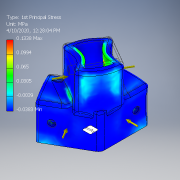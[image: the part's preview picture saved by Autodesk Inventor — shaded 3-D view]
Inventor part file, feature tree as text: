
AUTODESK INVENTOR PART (.ipt)
format: ipt  version: 2019.4 (Build 234330000, 330)  size: 473,600 bytes
history: native  units: mm
features: fillet x12, extrude x8, sketch x8
ambient origin geometry x8: Origin, YZ Plane, XZ Plane, XY Plane, X Axis, Y Axis, Z Axis, Center Point
bodies: Solid1 (feature_tree)
feature tree (28):
  extrude  "Extrusion1"  Depth=40.0mm
  extrude  "Extrusion9"  TaperAngle=60.0deg  [1 undecoded]
  extrude  "Extrusion10"  Depth=30.0mm TaperAngle=0.0deg
  extrude  "Extrusion11"  Depth=21.0mm
  extrude  "Extrusion12"  Depth=21.0mm TaperAngle=0.0deg
  extrude  "Extrusion13"  Depth=21.0mm
  extrude  "Extrusion14"  Depth=21.0mm TaperAngle=0.0deg
  extrude  "Extrusion15"  Depth=5.0mm
  fillet  "Fillet6"  Radius=30.0mm
  fillet  "Fillet7"  Radius=21.0mm
  fillet  "Fillet8"  Radius=21.0mm
  fillet  "Fillet9"  Radius=25.0mm
  fillet  "Fillet10"  Radius=10.0mm
  fillet  "Fillet11"  Radius=5.5mm
  fillet  "Fillet12"  Radius=30.0mm
  fillet  "Fillet13"  Radius=10.0mm
  fillet  "Fillet14"  Radius=5.5mm
  fillet  "Fillet15"  Radius=30.0mm
  fillet  "Fillet16"  Radius=10.0mm
  fillet  "Fillet17"  Radius=5.5mm
  sketch  "Sketch1"  dims[d1=30.0mm d2=40.0mm]
  sketch  "Sketch9"  dims[d3=30.0mm d4=60.0deg]
  sketch  "Sketch10"  dims[d5=40.0mm d6=30.0mm d7=0.0mm]
  sketch  "Sketch11"  dims[d41=15.0mm d42=21.0mm]
  sketch  "Sketch12"  dims[d43=21.0mm d44=25.0mm d45=0.0mm]
  sketch  "Sketch13"  dims[d46=15.0mm d47=21.0mm]
  sketch  "Sketch14"  dims[d48=21.0mm d49=25.0mm d50=0.0mm]
  sketch  "Sketch15"  dims[d51=30.0mm d52=30.0mm d53=30.0mm d54=0.0mm d55=21.0mm d56=21.0mm d57=25.0mm d58=0.0mm d59=10.0mm d60=5.5mm d61=30.0mm d62=0.0mm d63=10.0mm d64=5.5mm d65=30.0mm d66=0.0mm d67=10.0mm d68=5.5mm d69=30.0mm d70=0.0mm d71=5.0mm d72=5.0mm d73=5.0mm d74=5.0mm d75=2.0mm d76=2.0mm d77=2.0mm d78=2.0mm d79=2.0mm d80=2.0mm d81=2.0mm d82=5.0mm]
note: 1 required parameter value undecoded (feature->parameter linkage not recoverable at this tier; creation-order binding heuristic only, values carry confidence <= 0.55)
